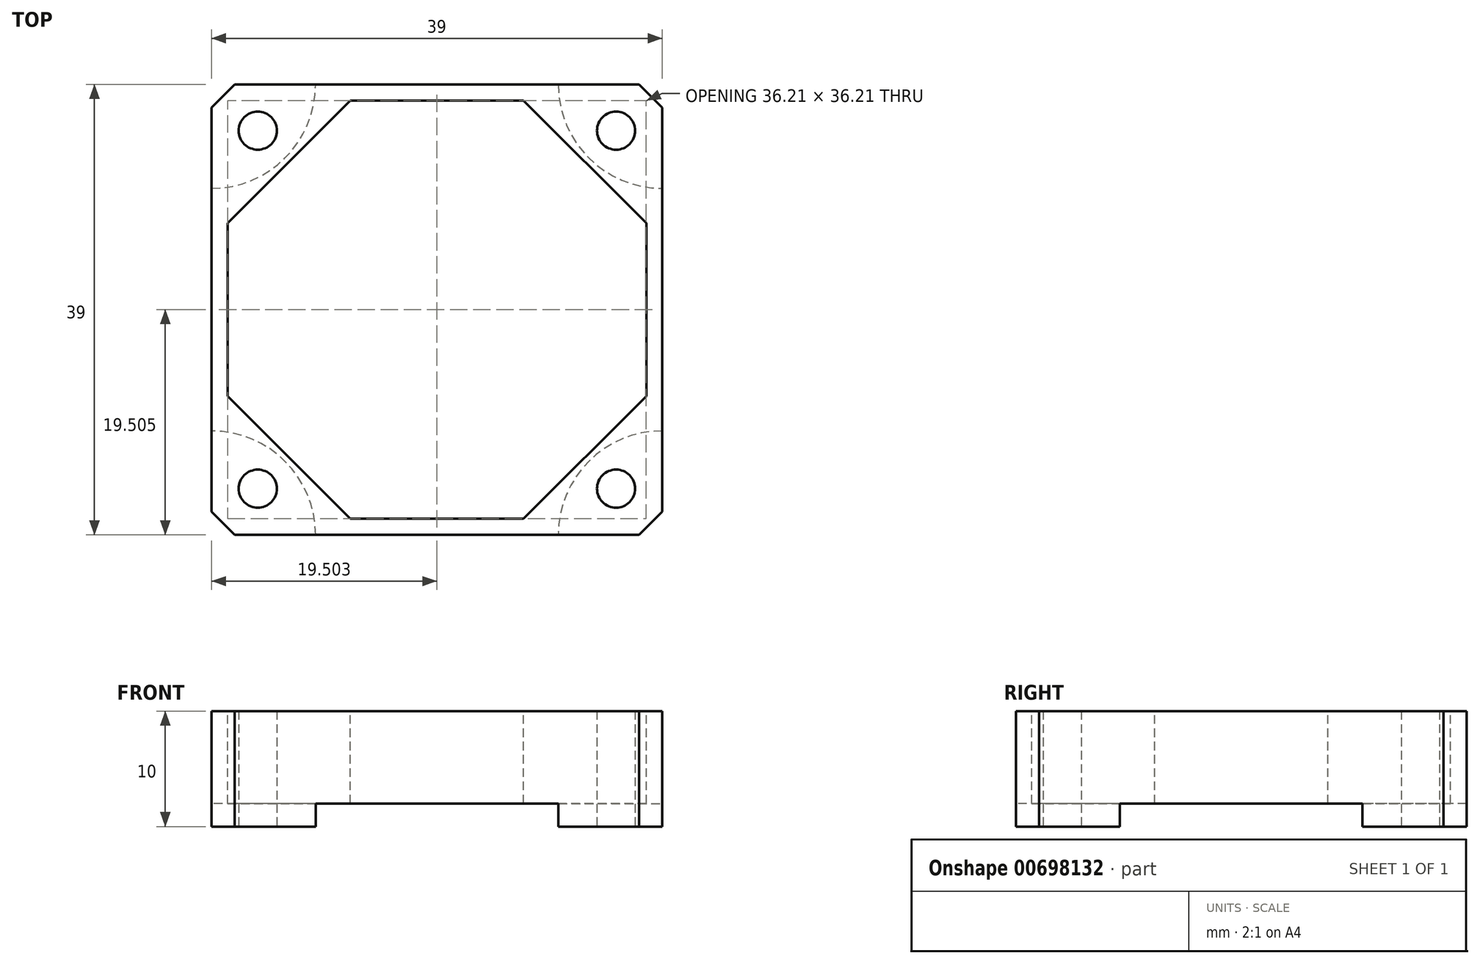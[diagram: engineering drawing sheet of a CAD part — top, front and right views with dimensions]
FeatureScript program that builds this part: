
annotation { "Feature Type Name" : "Feature", "Feature Type Description" : "" }
export const myFeature = defineFeature(function(context is Context, id is Id, definition is map)
    precondition{}
    {
        {
            var Q0;
            Q0=qCreatedBy(makeId("Top.planeOp"),FACE);
            var sketch = newSketch(context, id + "F0", { "sketchPlane" : qUnion([Q0])});
            skLineSegment(sketch, "E0.bottom", {"start": v(0.75, -13.33) * mm, "end": v(-38.25, -13.33) * mm});
            skLineSegment(sketch, "E0.top", {"start": v(0.75, 25.67) * mm, "end": v(-38.25, 25.67) * mm});
            skLineSegment(sketch, "E0.left", {"start": v(0.75, -13.33) * mm, "end": v(0.75, 25.67) * mm});
            skLineSegment(sketch, "E0.right", {"start": v(-38.25, -13.33) * mm, "end": v(-38.25, 25.67) * mm});
            skPoint(sketch, "E0.middle", {"position": v(-18.75, 6.17) * mm});
            skPoint(sketch, "E1", {"position": v(-34.25, 21.67) * mm});
            skPoint(sketch, "E2.1.0", {"position": v(-34.25, -9.33) * mm});
            skPoint(sketch, "E2.2.0", {"position": v(-3.25, -9.33) * mm});
            skPoint(sketch, "E2.3.0", {"position": v(-3.25, 21.67) * mm});
            skSolve(sketch);
        }
        {
            var Q0;
            Q0=makeQuery(id+"F0.imprint","IMPRINT",FACE,{"disambiguationData":[TD([[makeQuery(id+"F0.imprint","IMPRINT",EDGE,{"derivedFrom":sQuery(id+"F0.wireOp",EDGE,"E0.bottom")}),-1.0]])]});
            extrude(context, id + "F1", {"entities" : qUnion([Q0]), "depth" : 10 * mm, "offsetDistance" : 25 * mm});
        }
        {
            var Q0;
            Q0=makeQuery(id+"F0.imprint","IMPRINT",FACE,{"disambiguationData":[TD([[makeQuery(id+"F0.imprint","IMPRINT",EDGE,{"derivedFrom":sQuery(id+"F0.wireOp",EDGE,"E0.bottom")}),-1.0]])]});
            var sketch = newSketch(context, id + "F2", { "sketchPlane" : qUnion([Q0])});
            skLineSegment(sketch, "E3.0", {"start": v(0.75, -13.33) * mm, "end": v(0.75, 25.67) * mm});
            skPoint(sketch, "E3.1", {"position": v(0.75, 25.67) * mm});
            skLineSegment(sketch, "E3.2", {"start": v(0.75, 25.67) * mm, "end": v(-38.25, 25.67) * mm});
            skArc(sketch, "E4", {"start": v(0.75, 16.67) * mm, "mid": v(-5.61, 19.31) * mm, "end": v(-8.25, 25.67) * mm});
            skPoint(sketch, "E5.0", {"position": v(-18.75, 6.17) * mm});
            skArc(sketch, "E6.1.0", {"start": v(-29.25, 25.67) * mm, "mid": v(-31.88, 19.31) * mm, "end": v(-38.25, 16.67) * mm});
            skArc(sketch, "E6.2.0", {"start": v(-38.25, -4.33) * mm, "mid": v(-31.88, -6.96) * mm, "end": v(-29.25, -13.33) * mm});
            skArc(sketch, "E6.3.0", {"start": v(-8.25, -13.33) * mm, "mid": v(-5.61, -6.96) * mm, "end": v(0.75, -4.33) * mm});
            skSolve(sketch);
        }
        {
            var Q0;
            {var subQ3=sQuery(id+"F2.wireOp",EDGE,"E4");Q0=makeQuery(id+"F2.imprint","IMPRINT",FACE,{"disambiguationData":[TD([[makeQuery(id+"F2.imprint","IMPRINT",EDGE,{"derivedFrom":subQ3}),-1.0]])]});}
            var Q1;
            {var subQ3=sQuery(id+"F2.wireOp",EDGE,"E6.1.0");Q1=makeQuery(id+"F2.imprint","IMPRINT",FACE,{"disambiguationData":[TD([[makeQuery(id+"F2.imprint","IMPRINT",EDGE,{"derivedFrom":subQ3}),-1.0]])]});}
            var Q2;
            {var subQ0=sQuery(id+"F2.wireOp",EDGE,"E6.2.0");Q2=makeQuery(id+"F2.imprint","IMPRINT",FACE,{"disambiguationData":[TD([[makeQuery(id+"F2.imprint","IMPRINT",EDGE,{"derivedFrom":subQ0}),-1.0]])]});}
            var Q3;
            {var subQ3=sQuery(id+"F2.wireOp",EDGE,"E6.3.0");Q3=makeQuery(id+"F2.imprint","IMPRINT",FACE,{"disambiguationData":[TD([[makeQuery(id+"F2.imprint","IMPRINT",EDGE,{"derivedFrom":subQ3}),-1.0]])]});}
            extrude(context, id + "F3", {"entities" : qUnion([Q0, Q1, Q2, Q3]), "operationType" : NewBodyOperationType.REMOVE, "depth" : 2 * mm, "offsetDistance" : 25 * mm});
        }
        {
            var Q0;
            Q0=sQuery(id+"F0.wireOp",VERTEX,"E2.3.0");
            var Q1;
            Q1=sQuery(id+"F0.wireOp",VERTEX,"E1");
            var Q2;
            Q2=sQuery(id+"F0.wireOp",VERTEX,"E2.1.0");
            var Q3;
            Q3=sQuery(id+"F0.wireOp",VERTEX,"E2.2.0");
            var Q4;
            Q4=makeQuery(id+"F1.opExtrude","SWEPT_BODY",BODY,{"disambiguationData":[OSD([sQuery(id+"F0.wireOp",EDGE,"E0.bottom"),sQuery(id+"F0.wireOp",EDGE,"E0.top"),sQuery(id+"F0.wireOp",EDGE,"E0.left"),sQuery(id+"F0.wireOp",EDGE,"E0.right")])]});
            hole(context, id + "F4", {"style" : HoleStyle.SIMPLE, "endStyle" : HoleEndStyle.BLIND, "oppositeDirection" : true, "standardTappedOrClearance" : lookupTablePath({ "standard" : "ISO", "fit" : "Normal", "size" : "M3", "type" : "Clearance" }), "standardBlindInLast" : lookupTablePath({ "fit" : "Standard", "standard" : "ISO", "size" : "M3", "type" : "Clearance" }), "holeDiameter" : 3.3 * mm, "majorDiameter" : 5 * mm, "holeDepth" : 20 * mm, "isTappedThrough" : true, "tappedDepth" : 12 * mm, "tapClearance" : 3, "startFromSketch" : true, "locations" : qUnion([Q0, Q1, Q2, Q3]), "scope" : qUnion([Q4])});
        }
        {
            var Q0;
            Q0=makeQuery(id+"F1.opExtrude","SWEPT_EDGE",EDGE,{"disambiguationData":[OSD([sQuery(id+"F0.wireOp",EDGE,"E0.bottom"),sQuery(id+"F0.wireOp",EDGE,"E0.left")])]});
            var Q1;
            Q1=makeQuery(id+"F1.opExtrude","SWEPT_EDGE",EDGE,{"disambiguationData":[OSD([sQuery(id+"F0.wireOp",EDGE,"E0.top"),sQuery(id+"F0.wireOp",EDGE,"E0.left")])]});
            var Q2;
            Q2=makeQuery(id+"F1.opExtrude","SWEPT_EDGE",EDGE,{"disambiguationData":[OSD([sQuery(id+"F0.wireOp",EDGE,"E0.top"),sQuery(id+"F0.wireOp",EDGE,"E0.right")])]});
            var Q3;
            Q3=makeQuery(id+"F1.opExtrude","SWEPT_EDGE",EDGE,{"disambiguationData":[OSD([sQuery(id+"F0.wireOp",EDGE,"E0.bottom"),sQuery(id+"F0.wireOp",EDGE,"E0.right")])]});
            chamfer(context, id + "F5", {"entities" : qUnion([Q0, Q1, Q2, Q3]), "width" : 2 * mm, "tangentPropagation" : true});
        }
        {
            var Q0;
            Q0=makeQuery(id+"F1.opExtrude","CAP_FACE",FACE,{"disambiguationData":[OSD([sQuery(id+"F0.wireOp",EDGE,"E0.bottom"),sQuery(id+"F0.wireOp",EDGE,"E0.top"),sQuery(id+"F0.wireOp",EDGE,"E0.left"),sQuery(id+"F0.wireOp",EDGE,"E0.right")])],"isStart":false});
            var sketch = newSketch(context, id + "F6", { "sketchPlane" : qUnion([Q0])});
            skSolve(sketch);
        }
        {
            var Q0;
            {var subQ3=sQuery(id+"F0.wireOp",EDGE,"E0.bottom");Q0=makeQuery(id+"F6.imprint","IMPRINT",FACE,{"disambiguationData":[TD([[makeQuery(id+"F6.imprint","IMPRINT",EDGE,{"derivedFrom":makeQuery(id+"F1.opExtrude","CAP_EDGE",EDGE,{"disambiguationData":[OSD([subQ3])],"isStart":false})}),-1.0]])]});}
            var sketch = newSketch(context, id + "F7", { "sketchPlane" : qUnion([Q0])});
            skPoint(sketch, "E7.0", {"position": v(-18.75, 6.17) * mm});
            skCircle(sketch, "E8.cCircle", {"center": v(-18.75, 6.17) * mm, "radius": 19.6 * mm, "construction": true});
            skLineSegment(sketch, "E8.0", {"start": v(-0.64, -1.33) * mm, "end": v(-11.25, -11.93) * mm});
            skLineSegment(sketch, "E8.1", {"start": v(-11.25, -11.93) * mm, "end": v(-26.25, -11.93) * mm});
            skLineSegment(sketch, "E8.2", {"start": v(-26.25, -11.93) * mm, "end": v(-36.85, -1.33) * mm});
            skLineSegment(sketch, "E8.3", {"start": v(-36.85, -1.33) * mm, "end": v(-36.85, 13.67) * mm});
            skLineSegment(sketch, "E8.4", {"start": v(-36.85, 13.67) * mm, "end": v(-26.25, 24.28) * mm});
            skLineSegment(sketch, "E8.5", {"start": v(-26.25, 24.28) * mm, "end": v(-11.25, 24.28) * mm});
            skLineSegment(sketch, "E8.6", {"start": v(-11.25, 24.28) * mm, "end": v(-0.64, 13.67) * mm});
            skLineSegment(sketch, "E8.7", {"start": v(-0.64, 13.67) * mm, "end": v(-0.64, -1.33) * mm});
            skSolve(sketch);
        }
        {
            var Q0;
            Q0=makeQuery(id+"F7.imprint","IMPRINT",FACE,{"disambiguationData":[TD([[makeQuery(id+"F7.imprint","IMPRINT",EDGE,{"derivedFrom":sQuery(id+"F7.wireOp",EDGE,"E8.0")}),-1.0]])]});
            extrude(context, id + "F8", {"entities" : qUnion([Q0]), "operationType" : NewBodyOperationType.REMOVE, "oppositeDirection" : true, "depth" : 8 * mm, "offsetDistance" : 25 * mm});
        }
    });
